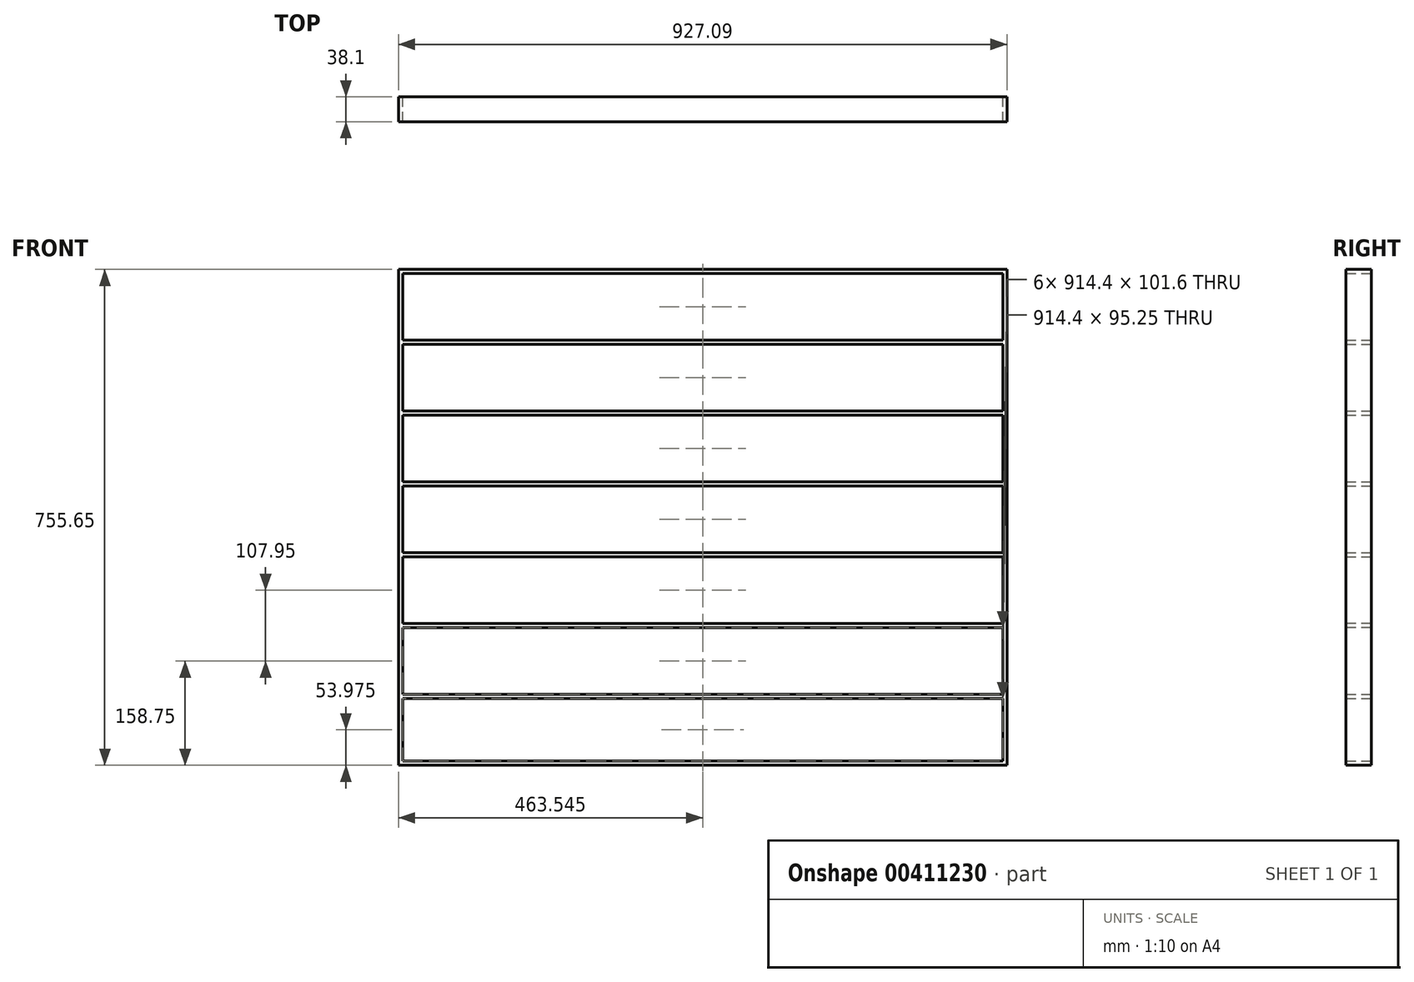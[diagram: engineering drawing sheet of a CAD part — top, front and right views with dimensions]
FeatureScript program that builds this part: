
annotation { "Feature Type Name" : "Feature", "Feature Type Description" : "" }
export const myFeature = defineFeature(function(context is Context, id is Id, definition is map)
    precondition{}
    {
        {
            var Q0;
            Q0=qCreatedBy(makeId("Top.planeOp"),FACE);
            var sketch = newSketch(context, id + "F0", { "sketchPlane" : qUnion([Q0])});
            skLineSegment(sketch, "E0.bottom", {"start": v(3.18, -19.05) * mm, "end": v(-3.17, -19.05) * mm});
            skLineSegment(sketch, "E0.top", {"start": v(3.17, 19.05) * mm, "end": v(-3.18, 19.05) * mm});
            skLineSegment(sketch, "E0.left", {"start": v(3.18, -19.05) * mm, "end": v(3.17, 19.05) * mm});
            skLineSegment(sketch, "E0.right", {"start": v(-3.17, -19.05) * mm, "end": v(-3.18, 19.05) * mm});
            skPoint(sketch, "E0.middle", {"position": v(0, 0) * mm});
            skSolve(sketch);
        }
        {
            var Q0;
            Q0 = qSketchRegion(id + "F0", true);
            extrude(context, id + "F1", {"entities" : qUnion([Q0]), "depth" : 755.65 * mm});
        }
        {
            var Q0;
            Q0=makeQuery(id+"F1.opExtrude","SWEPT_FACE",FACE,{"disambiguationData":[OSD([sQuery(id+"F0.wireOp",EDGE,"E0.left")])]});
            var sketch = newSketch(context, id + "F2", { "sketchPlane" : qUnion([Q0])});
            skLineSegment(sketch, "E1.bottom", {"start": v(-19.05, 101.6) * mm, "end": v(19.05, 101.6) * mm});
            skLineSegment(sketch, "E1.top", {"start": v(-19.05, 107.95) * mm, "end": v(19.05, 107.95) * mm});
            skLineSegment(sketch, "E1.left", {"start": v(-19.05, 101.6) * mm, "end": v(-19.05, 107.95) * mm});
            skLineSegment(sketch, "E1.right", {"start": v(19.05, 101.6) * mm, "end": v(19.05, 107.95) * mm});
            skPoint(sketch, "E1.middle", {"position": v(0, 104.78) * mm});
            skLineSegment(sketch, "E2.bottom", {"start": v(-19.05, 0) * mm, "end": v(19.05, 0) * mm});
            skLineSegment(sketch, "E2.top", {"start": v(-19.05, 6.35) * mm, "end": v(19.05, 6.35) * mm});
            skLineSegment(sketch, "E2.left", {"start": v(-19.05, 0) * mm, "end": v(-19.05, 6.35) * mm});
            skLineSegment(sketch, "E2.right", {"start": v(19.05, 0) * mm, "end": v(19.05, 6.35) * mm});
            skLineSegment(sketch, "E3.bottom", {"start": v(19.05, 215.9) * mm, "end": v(-19.05, 215.9) * mm});
            skLineSegment(sketch, "E3.top", {"start": v(19.05, 209.55) * mm, "end": v(-19.05, 209.55) * mm});
            skLineSegment(sketch, "E3.left", {"start": v(19.05, 215.9) * mm, "end": v(19.05, 209.55) * mm});
            skLineSegment(sketch, "E3.right", {"start": v(-19.05, 215.9) * mm, "end": v(-19.05, 209.55) * mm});
            skPoint(sketch, "E3.middle", {"position": v(0, 212.72) * mm});
            skLineSegment(sketch, "E4.bottom", {"start": v(-19.05, 317.5) * mm, "end": v(19.05, 317.5) * mm});
            skLineSegment(sketch, "E4.top", {"start": v(-19.05, 323.85) * mm, "end": v(19.05, 323.85) * mm});
            skLineSegment(sketch, "E4.left", {"start": v(-19.05, 317.5) * mm, "end": v(-19.05, 323.85) * mm});
            skLineSegment(sketch, "E4.right", {"start": v(19.05, 317.5) * mm, "end": v(19.05, 323.85) * mm});
            skPoint(sketch, "E4.middle", {"position": v(0, 320.68) * mm});
            skLineSegment(sketch, "E5.bottom", {"start": v(-19.05, 425.45) * mm, "end": v(19.05, 425.45) * mm});
            skLineSegment(sketch, "E5.top", {"start": v(-19.05, 431.8) * mm, "end": v(19.05, 431.8) * mm});
            skLineSegment(sketch, "E5.left", {"start": v(-19.05, 425.45) * mm, "end": v(-19.05, 431.8) * mm});
            skLineSegment(sketch, "E5.right", {"start": v(19.05, 425.45) * mm, "end": v(19.05, 431.8) * mm});
            skPoint(sketch, "E5.middle", {"position": v(0, 428.62) * mm});
            skLineSegment(sketch, "E6.bottom", {"start": v(-19.05, 533.4) * mm, "end": v(19.05, 533.4) * mm});
            skLineSegment(sketch, "E6.top", {"start": v(-19.05, 539.75) * mm, "end": v(19.05, 539.75) * mm});
            skLineSegment(sketch, "E6.left", {"start": v(-19.05, 533.4) * mm, "end": v(-19.05, 539.75) * mm});
            skLineSegment(sketch, "E6.right", {"start": v(19.05, 533.4) * mm, "end": v(19.05, 539.75) * mm});
            skPoint(sketch, "E6.middle", {"position": v(0, 536.58) * mm});
            skLineSegment(sketch, "E7.bottom", {"start": v(-19.05, 641.35) * mm, "end": v(19.05, 641.35) * mm});
            skLineSegment(sketch, "E7.top", {"start": v(-19.05, 647.7) * mm, "end": v(19.05, 647.7) * mm});
            skLineSegment(sketch, "E7.left", {"start": v(-19.05, 641.35) * mm, "end": v(-19.05, 647.7) * mm});
            skLineSegment(sketch, "E7.right", {"start": v(19.05, 641.35) * mm, "end": v(19.05, 647.7) * mm});
            skPoint(sketch, "E7.middle", {"position": v(0, 644.53) * mm});
            skLineSegment(sketch, "E8.bottom", {"start": v(-19.05, 749.3) * mm, "end": v(19.05, 749.3) * mm});
            skLineSegment(sketch, "E8.top", {"start": v(-19.05, 755.65) * mm, "end": v(19.05, 755.65) * mm});
            skLineSegment(sketch, "E8.left", {"start": v(-19.05, 749.3) * mm, "end": v(-19.05, 755.65) * mm});
            skLineSegment(sketch, "E8.right", {"start": v(19.05, 749.3) * mm, "end": v(19.05, 755.65) * mm});
            skPoint(sketch, "E8.middle", {"position": v(0, 752.48) * mm});
            skSolve(sketch);
        }
        {
            var Q0;
            Q0 = qSketchRegion(id + "F2", true);
            extrude(context, id + "F3", {"entities" : qUnion([Q0]), "operationType" : NewBodyOperationType.ADD, "depth" : 457.2 * mm});
        }
        {
            var Q0;
            Q0=makeQuery(id+"F1.opExtrude","SWEPT_BODY",BODY,{"disambiguationData":[OSD([sQuery(id+"F0.wireOp",EDGE,"E0.bottom"),sQuery(id+"F0.wireOp",EDGE,"E0.top"),sQuery(id+"F0.wireOp",EDGE,"E0.left"),sQuery(id+"F0.wireOp",EDGE,"E0.right")])]});
            var Q1;
            Q1=makeQuery(id+"F3.opExtrude","CAP_FACE",FACE,{"disambiguationData":[OSD([sQuery(id+"F2.wireOp",EDGE,"E7.bottom"),sQuery(id+"F2.wireOp",EDGE,"E7.top"),sQuery(id+"F2.wireOp",EDGE,"E7.left"),sQuery(id+"F2.wireOp",EDGE,"E7.right")])],"isStart":false});
            mirror(context, id + "F4", {"operationType" : NewBodyOperationType.ADD, "entities" : qUnion([Q0]), "mirrorPlane" : qUnion([Q1])});
        }
    });
